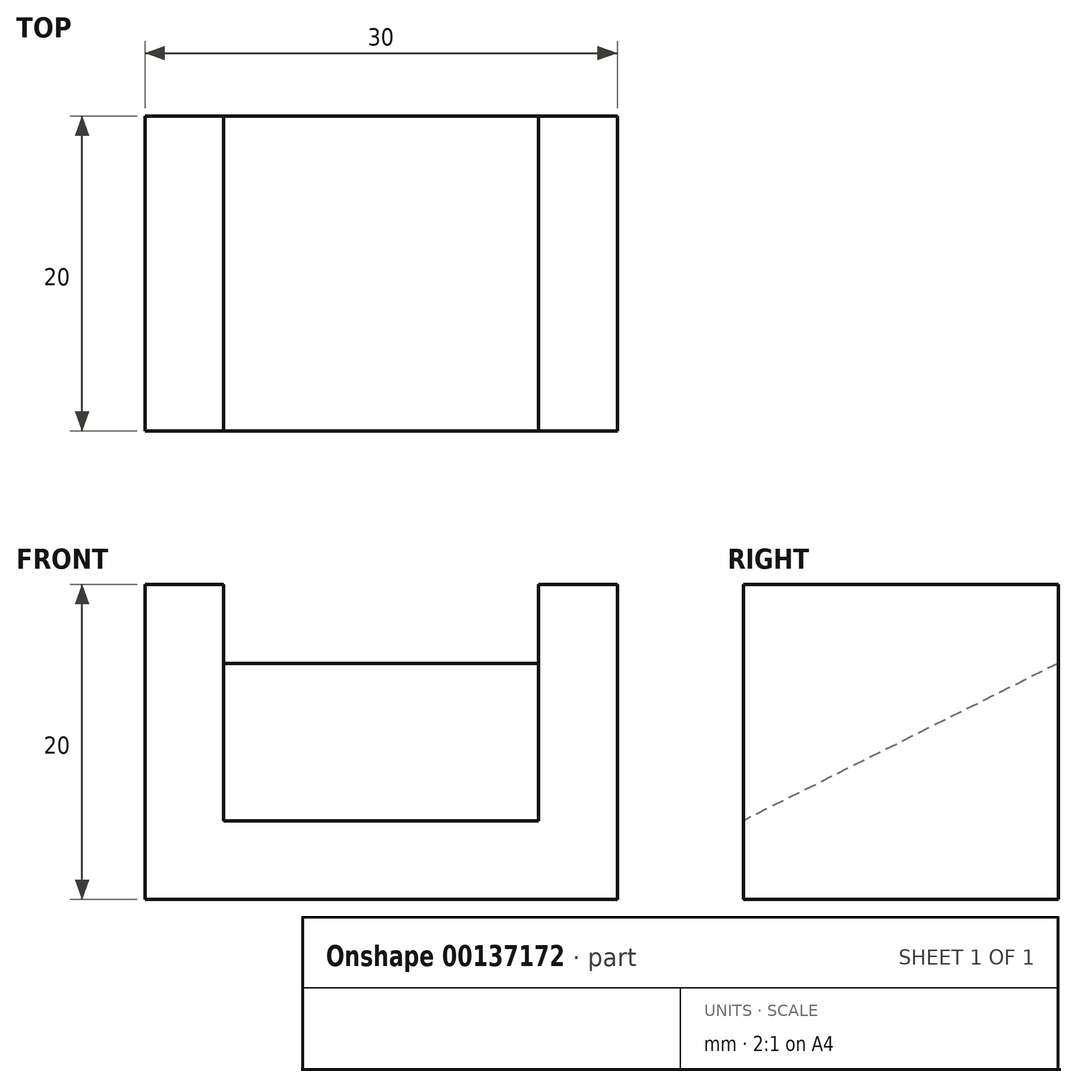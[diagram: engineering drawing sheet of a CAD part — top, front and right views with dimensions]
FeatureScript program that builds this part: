
annotation { "Feature Type Name" : "Feature", "Feature Type Description" : "" }
export const myFeature = defineFeature(function(context is Context, id is Id, definition is map)
    precondition{}
    {
        {
            var Q0;
            Q0=qCreatedBy(makeId("Front.planeOp"),FACE);
            var sketch = newSketch(context, id + "F0", { "sketchPlane" : qUnion([Q0])});
            skLineSegment(sketch, "E0.bottom", {"start": v(-13.87, 20) * mm, "end": v(16.13, 20) * mm});
            skLineSegment(sketch, "E0.top", {"start": v(-13.87, 0) * mm, "end": v(16.13, 0) * mm});
            skLineSegment(sketch, "E0.left", {"start": v(-13.87, 20) * mm, "end": v(-13.87, 0) * mm});
            skLineSegment(sketch, "E0.right", {"start": v(16.13, 20) * mm, "end": v(16.13, 0) * mm});
            skSolve(sketch);
        }
        {
            var Q0;
            Q0 = qSketchRegion(id + "F0", true);
            extrude(context, id + "F1", {"entities" : qUnion([Q0]), "depth" : 20 * mm});
        }
        {
            var Q0;
            Q0=qCreatedBy(makeId("Top.planeOp"),FACE);
            var sketch = newSketch(context, id + "F2", { "sketchPlane" : qUnion([Q0])});
            skLineSegment(sketch, "E1.bottom", {"start": v(-8.87, 0) * mm, "end": v(11.13, 0) * mm});
            skLineSegment(sketch, "E1.top", {"start": v(-8.87, -20) * mm, "end": v(11.13, -20) * mm});
            skLineSegment(sketch, "E1.left", {"start": v(-8.87, 0) * mm, "end": v(-8.87, -20) * mm});
            skLineSegment(sketch, "E1.right", {"start": v(11.13, 0) * mm, "end": v(11.13, -20) * mm});
            skSolve(sketch);
        }
        {
            var Q0;
            Q0 = qSketchRegion(id + "F2", true);
            extrude(context, id + "F3", {"entities" : qUnion([Q0]), "operationType" : NewBodyOperationType.REMOVE, "depth" : 20 * mm, "hasSecondDirection" : true, "secondDirectionOppositeDirection" : false, "secondDirectionDepth" : 5 * mm});
        }
        {
            var Q0;
            Q0=qCreatedBy(makeId("Right.planeOp"),FACE);
            var sketch = newSketch(context, id + "F4", { "sketchPlane" : qUnion([Q0])});
            skLineSegment(sketch, "E2", {"start": v(-20, 0) * mm, "end": v(-20, 5) * mm});
            skLineSegment(sketch, "E3", {"start": v(-20, 5) * mm, "end": v(0, 15) * mm});
            skLineSegment(sketch, "E4", {"start": v(-20, 0) * mm, "end": v(0, 0) * mm});
            skLineSegment(sketch, "E5", {"start": v(0, 0) * mm, "end": v(0, 15) * mm});
            skSolve(sketch);
        }
        {
            var Q0;
            Q0 = qSketchRegion(id + "F4", true);
            extrude(context, id + "F5", {"entities" : qUnion([Q0]), "operationType" : NewBodyOperationType.ADD, "endBound" : BoundingType.SYMMETRIC, "depth" : 25 * mm});
        }
    });
